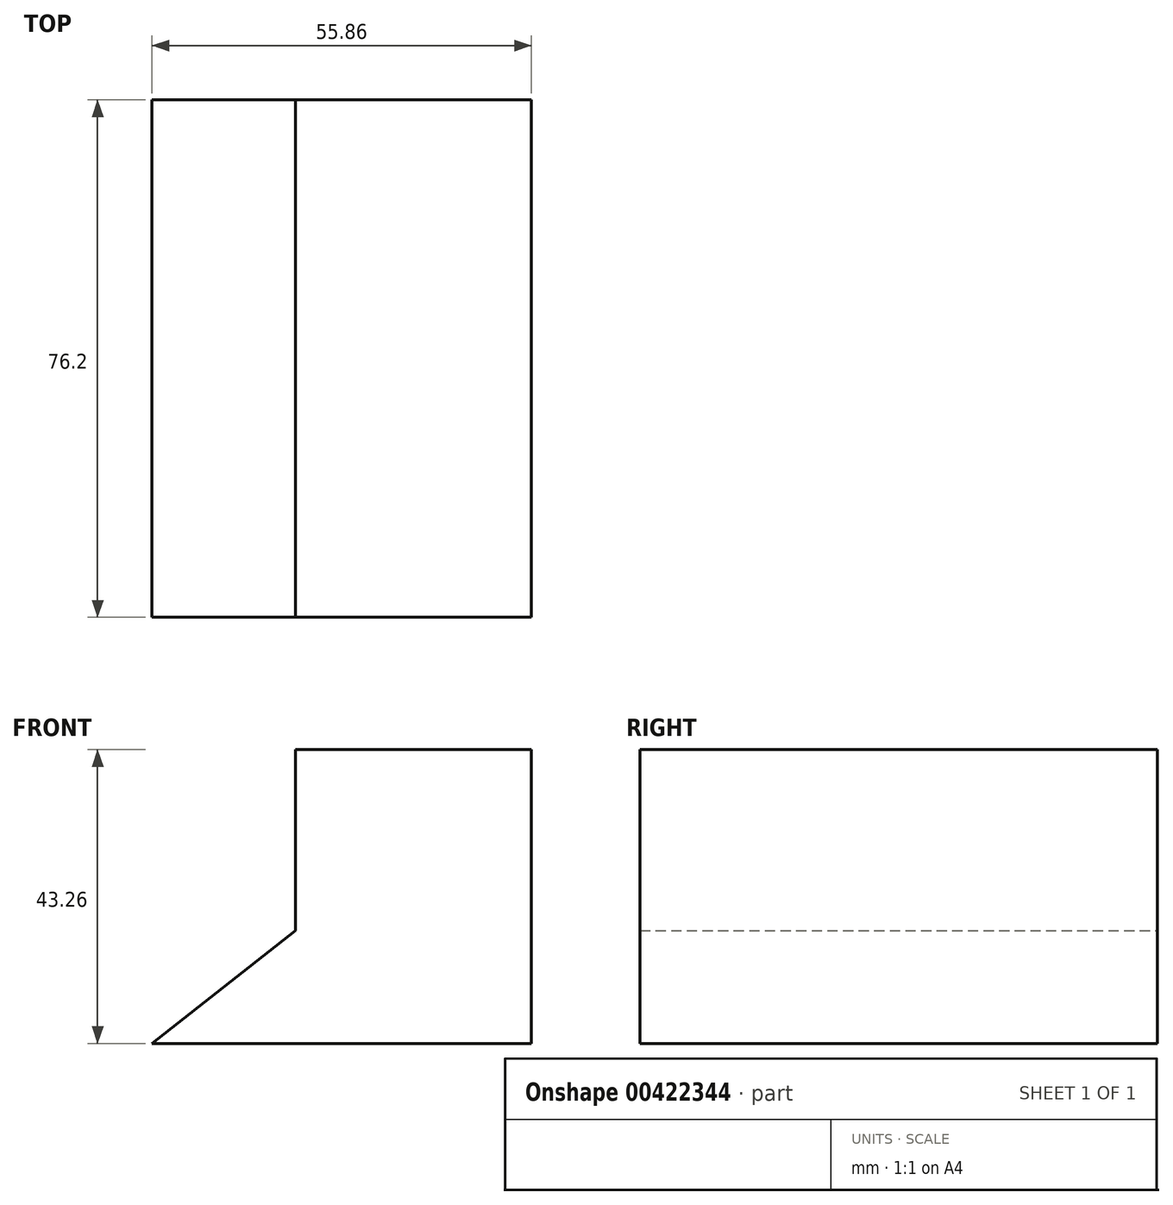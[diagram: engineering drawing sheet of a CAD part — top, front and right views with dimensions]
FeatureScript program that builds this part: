
annotation { "Feature Type Name" : "Feature", "Feature Type Description" : "" }
export const myFeature = defineFeature(function(context is Context, id is Id, definition is map)
    precondition{}
    {
        {
            var Q0;
            Q0=qCreatedBy(makeId("Front.planeOp"),FACE);
            var sketch = newSketch(context, id + "F0", { "sketchPlane" : qUnion([Q0])});
            skLineSegment(sketch, "E0", {"start": v(0, 0) * mm, "end": v(-55.86, 0) * mm});
            skLineSegment(sketch, "E1", {"start": v(-55.86, 0) * mm, "end": v(-34.72, 16.6) * mm});
            skLineSegment(sketch, "E2", {"start": v(-34.72, 16.6) * mm, "end": v(-34.72, 43.26) * mm});
            skLineSegment(sketch, "E3", {"start": v(-34.72, 43.26) * mm, "end": v(0, 43.26) * mm});
            skLineSegment(sketch, "E4", {"start": v(0, 43.26) * mm, "end": v(0, 0) * mm});
            skSolve(sketch);
        }
        {
            var Q0;
            Q0 = qSketchRegion(id + "F0", true);
            extrude(context, id + "F1", {"entities" : qUnion([Q0]), "depth" : 76.2 * mm});
        }
    });
